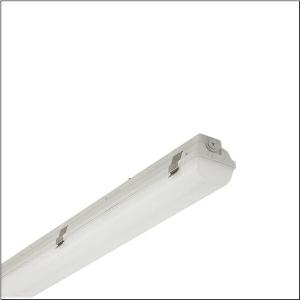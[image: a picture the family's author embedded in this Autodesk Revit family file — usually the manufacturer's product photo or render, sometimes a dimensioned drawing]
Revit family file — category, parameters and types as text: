
# Revit family: monsun_r__21_eco_51fj10mp47a_2b6f
name_source: partatom
category: Lighting Fixtures
units: mm (PartAtom-declared; Revit-internal decimal feet)

## family parameters
Cut with Voids When Loaded = No
Host = Face
Light Source = No
Part Type = Normal
Room Calculation Point = No
Round Connector Dimension = Use Diameter
Shared = No

## types (1)
- --- (1 x LED, 7000 lm, 50 W, 4000K)
    Apparent Load = 50 VA
    CIE Flux Codes = 41 70 89 90 100
    Color Rendering = 80
    Color Temperature = 4000K
    Default Elevation = 1800 mm
    Description = Monsun® 21 Eco, damp-proof luminaire, primary optical cover: diffuser, of PMMA, frosted, light emission: direct distribution, primary light characteristic: symmetric, installation type: suspended mounting, surface-mounted, LED, rated luminous flux: 7.000lm, luminous efficacy: 140lm/W, light colour: 840, colour temperature: 4000K, control gear: ECG Multilumen, with terminal, 3-pole, max. 2.5mm², mains connection: 220..240V, AC, 50/60Hz, rated input power: 50W, housing, of glass-fibre reinforced polyester, light grey (RAL 7035), length: 1.577mm, width: 90mm, height: 95mm, clip for enclosure, of spring steel V2A, protection rating (complete): IP66, insulation class (complete): insulation class I (protective earthing), certification: CE, UKCA, protection symbol: D, impact resistance: IK02, permissible operating ambient temperature: -20..+35°C, corresponds to IFS (International Featured Standards) requirements for safety and quality in the food industry, contact your sales advisor before using the luminaires in applications with unclear chemical exposure, large temperature fluctuations or condensation-forming humidity, packaging unit: 1 piece
    Height = 103 mm
    Lamp = 1 x LED
    Lamp Light Flux = 7000 lm
    Lamp Power = 50 W
    Lamp count = 1
    Length = 1577 mm
    Luminous efficacy = 140 lm/W
    Manufacturer = Siteco
    ModVariant = No
    Model = 51FJ10MP47A
    Mounting Place = Ceiling
    Mounting Type = Surface mounted
    Number of Poles = 1
    OnlyDefault = Yes
    Power Factor = 1
    Product Name = Monsun® 21 Eco
    Product group = damp-proof luminaire
    ProductGroupID = 301
    Protection Class = Protection class I
    Protection Degree = IP 66
    RLX_Detail_Level = 1
    RLX_Emergency_Light_Flux = 0 lm
    RLX_Emergency_Type = 0
    RLX_Emergency_Type_DB = No
    RlxData = <blob elided: 34089 chars, md5=ed7a3255>
    Socket = socket
    Standby Power = 0 W
    System Light Flux = 7000 lm
    System Power = 50 W
    Type Comments = factory setting: luminous flux: 100 % | (ON | ON | ON | ON) | 350 mA
    Type Image = l_1007218.jpg
    URL = http://relux.com
    VarID = @adj_095769
    Voltage = 0 V
    Weight = 0.00 kg
    Width = 90 mm

## geometry (parser evidence)
native form markers: Blend x4, Sweep x12
no freeform markers — native parametric forms only
